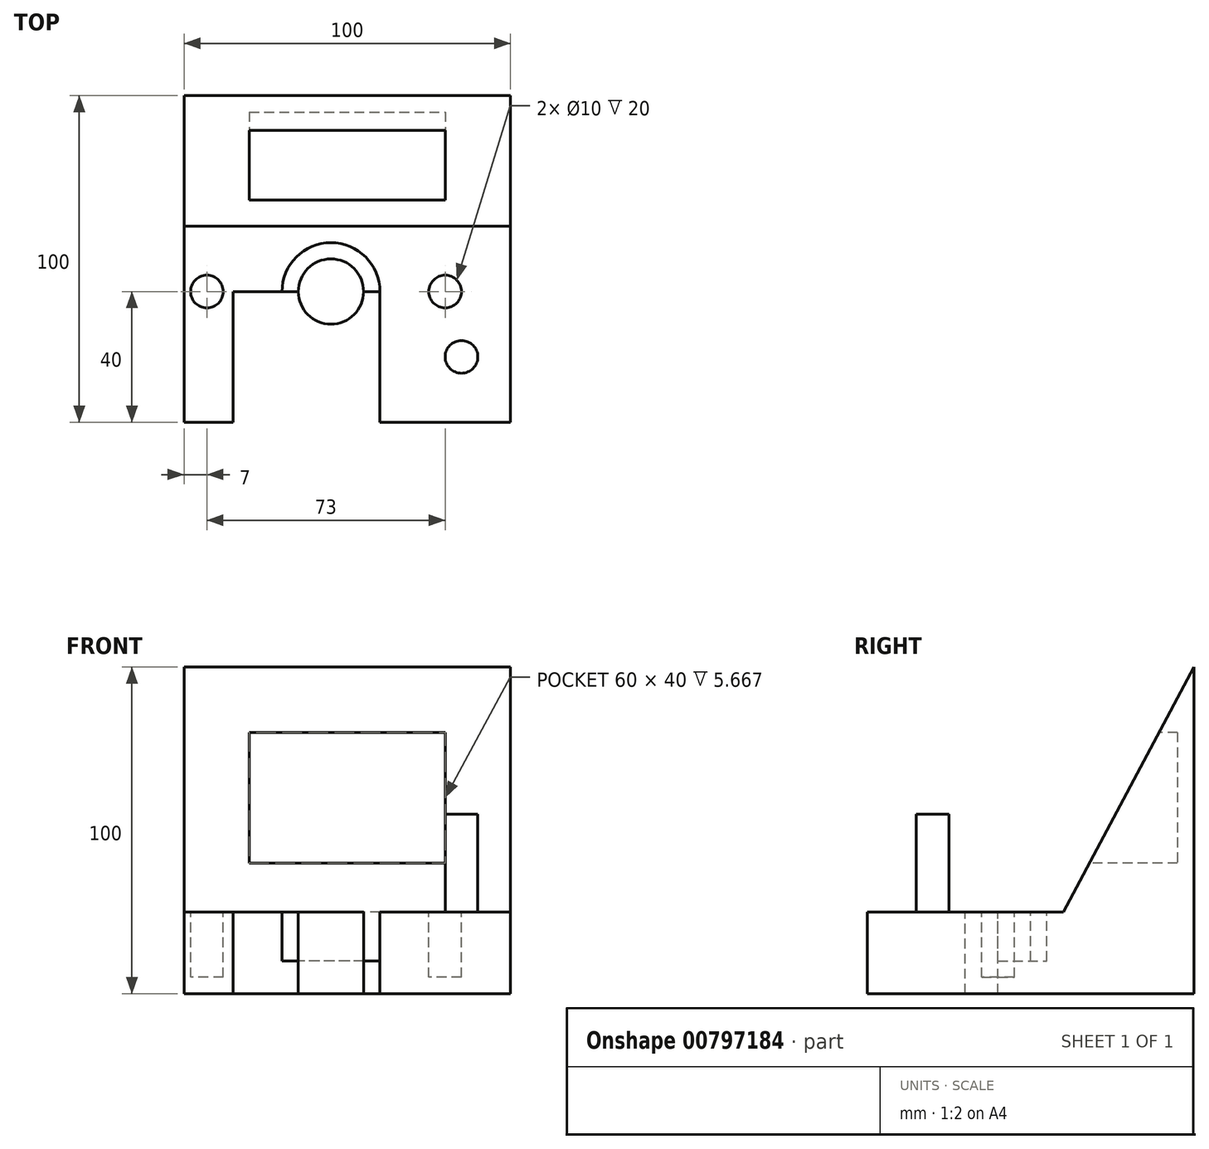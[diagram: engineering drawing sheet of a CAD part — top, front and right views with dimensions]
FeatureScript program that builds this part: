
annotation { "Feature Type Name" : "Feature", "Feature Type Description" : "" }
export const myFeature = defineFeature(function(context is Context, id is Id, definition is map)
    precondition{}
    {
        {
            var Q0;
            Q0=qCreatedBy(makeId("Right.planeOp"),FACE);
            var sketch = newSketch(context, id + "F0", { "sketchPlane" : qUnion([Q0])});
            skLineSegment(sketch, "E0", {"start": v(0, 0) * mm, "end": v(100, 0) * mm});
            skLineSegment(sketch, "E1", {"start": v(100, 0) * mm, "end": v(100, 100) * mm});
            skLineSegment(sketch, "E2", {"start": v(100, 100) * mm, "end": v(60, 25) * mm});
            skLineSegment(sketch, "E3", {"start": v(60, 25) * mm, "end": v(0, 25) * mm});
            skLineSegment(sketch, "E4", {"start": v(0, 25) * mm, "end": v(0, 0) * mm});
            skSolve(sketch);
        }
        {
            var Q0;
            Q0 = qSketchRegion(id + "F0", true);
            extrude(context, id + "F1", {"entities" : qUnion([Q0]), "depth" : 100 * mm, "offsetDistance" : 25 * mm});
        }
        {
            var Q0;
            Q0=makeQuery(id+"F1.opExtrude","SWEPT_FACE",FACE,{"disambiguationData":[OSD([sQuery(id+"F0.wireOp",EDGE,"E3")])]});
            var sketch = newSketch(context, id + "F2", { "sketchPlane" : qUnion([Q0])});
            skCircle(sketch, "E5", {"center": v(85, 20) * mm, "radius": 5 * mm});
            skSolve(sketch);
        }
        {
            var Q0;
            Q0 = qSketchRegion(id + "F2", true);
            extrude(context, id + "F3", {"entities" : qUnion([Q0]), "operationType" : NewBodyOperationType.ADD, "depth" : 30 * mm, "offsetDistance" : 25 * mm});
        }
        {
            var Q0;
            Q0=makeQuery(id+"F1.opExtrude","SWEPT_FACE",FACE,{"disambiguationData":[OSD([sQuery(id+"F0.wireOp",EDGE,"E3")])]});
            var sketch = newSketch(context, id + "F4", { "sketchPlane" : qUnion([Q0])});
            skCircle(sketch, "E6", {"center": v(7, 40) * mm, "radius": 5 * mm});
            skCircle(sketch, "E7", {"center": v(80, 40) * mm, "radius": 5 * mm});
            skSolve(sketch);
        }
        {
            var Q0;
            Q0 = qSketchRegion(id + "F4", true);
            extrude(context, id + "F5", {"entities" : qUnion([Q0]), "operationType" : NewBodyOperationType.REMOVE, "oppositeDirection" : true, "depth" : 20 * mm, "offsetDistance" : 25 * mm});
        }
        {
            var Q0;
            Q0=qCreatedBy(makeId("Front.planeOp"),FACE);
            var sketch = newSketch(context, id + "F6", { "sketchPlane" : qUnion([Q0])});
            skLineSegment(sketch, "E8.bottom", {"start": v(20, 80) * mm, "end": v(80, 80) * mm});
            skLineSegment(sketch, "E8.top", {"start": v(20, 40) * mm, "end": v(80, 40) * mm});
            skLineSegment(sketch, "E8.left", {"start": v(20, 80) * mm, "end": v(20, 40) * mm});
            skLineSegment(sketch, "E8.right", {"start": v(80, 80) * mm, "end": v(80, 40) * mm});
            skSolve(sketch);
        }
        {
            var Q0;
            Q0 = qSketchRegion(id + "F6", true);
            extrude(context, id + "F7", {"entities" : qUnion([Q0]), "operationType" : NewBodyOperationType.REMOVE, "oppositeDirection" : true, "depth" : 95 * mm, "offsetDistance" : 25 * mm});
        }
        {
            var Q0;
            Q0=makeQuery(id+"F1.opExtrude","SWEPT_FACE",FACE,{"disambiguationData":[OSD([sQuery(id+"F0.wireOp",EDGE,"E3")])]});
            var sketch = newSketch(context, id + "F8", { "sketchPlane" : qUnion([Q0])});
            skLineSegment(sketch, "E9.bottom", {"start": v(15, 0) * mm, "end": v(60, 0) * mm});
            skLineSegment(sketch, "E9.top", {"start": v(15, 40) * mm, "end": v(60, 40) * mm});
            skLineSegment(sketch, "E9.left", {"start": v(15, 0) * mm, "end": v(15, 40) * mm});
            skLineSegment(sketch, "E9.right", {"start": v(60, 0) * mm, "end": v(60, 40) * mm});
            skSolve(sketch);
        }
        {
            var Q0;
            Q0 = qSketchRegion(id + "F8", true);
            extrude(context, id + "F9", {"entities" : qUnion([Q0]), "operationType" : NewBodyOperationType.REMOVE, "oppositeDirection" : true, "depth" : 25 * mm, "offsetDistance" : 25 * mm});
        }
        {
            var Q0;
            Q0=makeQuery(id+"F1.opExtrude","SWEPT_FACE",FACE,{"disambiguationData":[OSD([sQuery(id+"F0.wireOp",EDGE,"E3")])]});
            var sketch = newSketch(context, id + "F10", { "sketchPlane" : qUnion([Q0])});
            skCircle(sketch, "E10", {"center": v(45, 40) * mm, "radius": 15 * mm});
            skSolve(sketch);
        }
        {
            var Q0;
            Q0 = qSketchRegion(id + "F10", true);
            extrude(context, id + "F11", {"entities" : qUnion([Q0]), "operationType" : NewBodyOperationType.REMOVE, "oppositeDirection" : true, "depth" : 15 * mm, "offsetDistance" : 25 * mm});
        }
        {
            var Q0;
            Q0=makeQuery(id+"F1.opExtrude","SWEPT_FACE",FACE,{"disambiguationData":[OSD([sQuery(id+"F0.wireOp",EDGE,"E3")])]});
            var sketch = newSketch(context, id + "F12", { "sketchPlane" : qUnion([Q0])});
            skCircle(sketch, "E11", {"center": v(45, 40) * mm, "radius": 10 * mm});
            skSolve(sketch);
        }
        {
            var Q0;
            Q0 = qSketchRegion(id + "F12", true);
            extrude(context, id + "F13", {"entities" : qUnion([Q0]), "operationType" : NewBodyOperationType.ADD, "oppositeDirection" : true, "depth" : 25 * mm, "offsetDistance" : 25 * mm});
        }
    });
